# Revit family: 230652KC-005-KMCS122R_230652KC-005-KMCS122RPSBS
name_source: partatom
category: Specialty Equipment
units: mm (PartAtom-declared; Revit-internal decimal feet)

## family parameters
Always vertical = Yes
Cut with Voids When Loaded = No
Enable Cutting in Views = No
Maintain Annotation Orientation = No
Part Type = Normal
Room Calculation Point = No
Round Connector Dimension = Use Diameter
Shared = No
Work Plane-Based = No

## types (2) — shared parameters
Accent Material = ARCAT - Metal - Steel - Stainless
Amps = 15 A
Back Panel Material = ARCAT - Metal - Aluminum
Body Material = ARCAT - Metal - Steel - Black
Clearance Material = ARCAT - Clearance
Depth = 18.31 "
Description = KitchenAid® Countertop Microwave
Display Panel Material = ARCAT - Plastic - Gray
Door Age = ARCAT - Metal - Steel - Aluminium - Green
Door Glass = ARCAT - Glass - Tempered - Dark Gray
Door Material = ARCAT - Metal - Steel - Gray
Energy Guide = N/A (not an energy product)
Family Name = Texas Combo Phase 2
Feature 1 = Auto Functions
Feature 2 = Steam Clean Function
Feature 3 = 1.6 Cu. Ft. Capacity
Glass Material = ARCAT - Glass - Tempered - Dark Black
Handle Material = ARCAT - Metal - Steel - Gray - Dark
Height = 12.25 "
Hz = 60 "
Leg Material = ARCAT - Metal - Steel - Black
Logo Material = Stainless Steel
Voltage = 120 V
Watts = 1700 "
Width = 21.75 "
zero-valued in all types: Default Elevation

## per-type parameters (varying)
| type | Dimension Guide | Door Frame | Installation-Fabrication |
| KMCS122RPS | The guide is not yet created since it's not required for a launch - dimension info can be found in the sales release if helpful: 
The guide is not yet created since it's not required for a launch - dimension info can be found in the sales release if helpful: 
The guide is not yet created since it's not required for a launch - dimension info can be found in the sales release if helpful: 
The guide is not yet created since it's not required for a launch - dimension info can be found in the sales release if helpful: | ARCAT - Metal - Steel - Aluminium(1) | https://drive.google.com
https://drive.google.com |
| KMCS122RBS | The guide is not yet created since it's not required for a launch - dimension info can be found in the sales release if helpful: | ARCAT - Metal - Steel - Golden | https://drive.google.com |

## geometry (parser evidence)
native form markers: Sweep x33
no freeform markers — native parametric forms only
